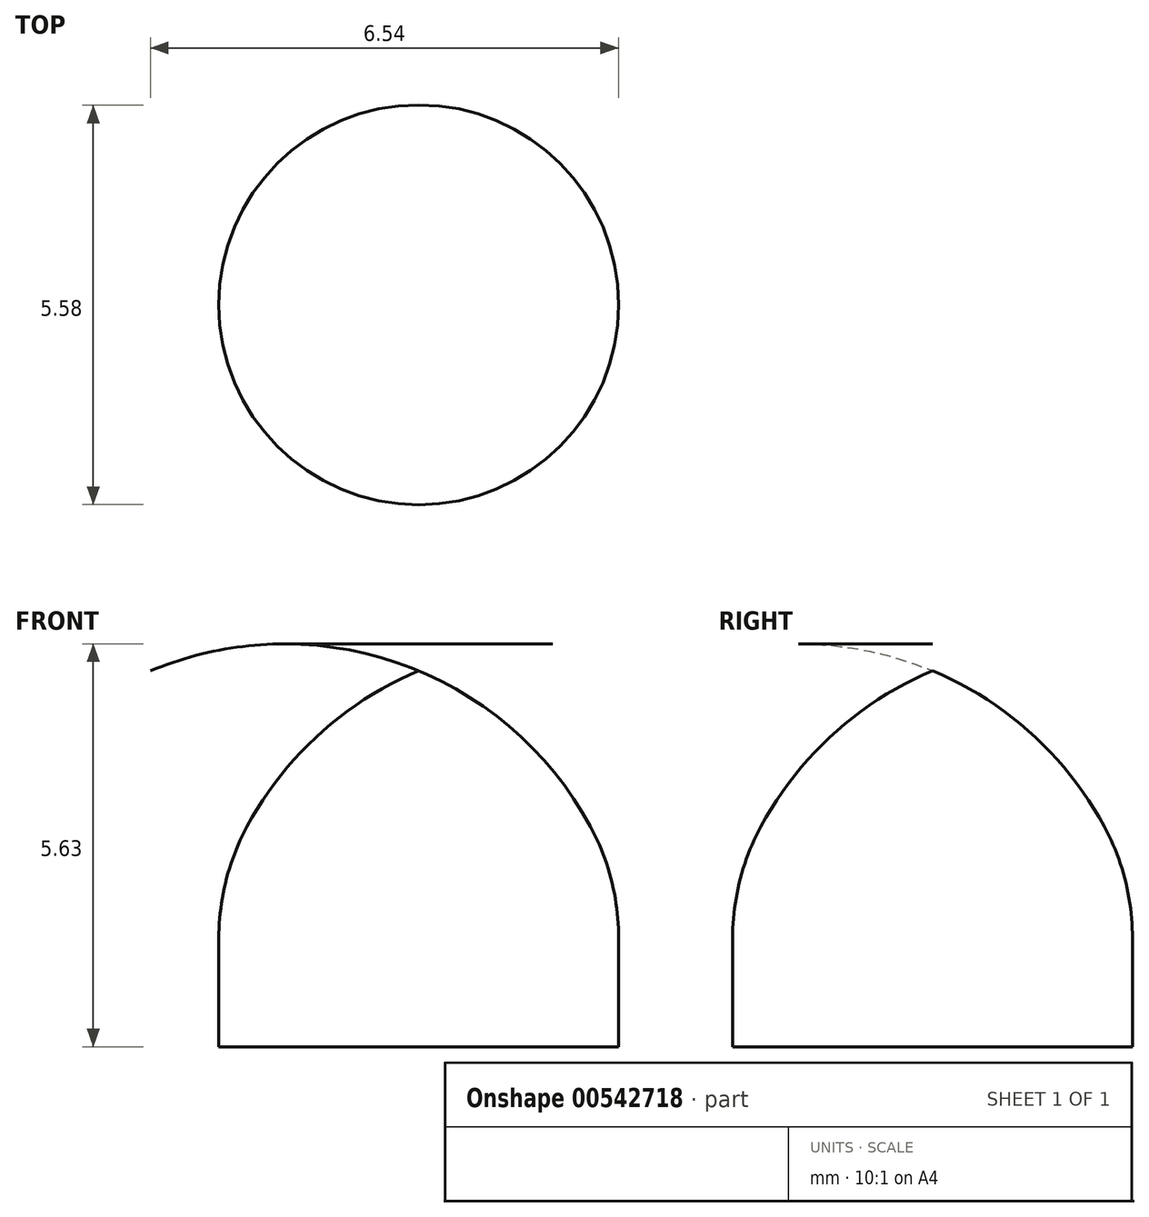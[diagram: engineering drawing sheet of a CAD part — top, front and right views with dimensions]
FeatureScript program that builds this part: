
annotation { "Feature Type Name" : "Feature", "Feature Type Description" : "" }
export const myFeature = defineFeature(function(context is Context, id is Id, definition is map)
    precondition{}
    {
        {
            var Q0;
            Q0=qCreatedBy(makeId("Front.planeOp"),FACE);
            var sketch = newSketch(context, id + "F0", { "sketchPlane" : qUnion([Q0])});
            skLineSegment(sketch, "E0", {"start": v(0, 0) * mm, "end": v(0, 5.25) * mm});
            skLineSegment(sketch, "E1", {"start": v(0, 0) * mm, "end": v(-2.8, 0) * mm});
            skLineSegment(sketch, "E2", {"start": v(-2.8, 0) * mm, "end": v(-2.8, 2.1) * mm});
            skArc(sketch, "E3", {"start": v(0, 5.25) * mm, "mid": v(-1.76, 4) * mm, "end": v(-2.8, 2.1) * mm});
            skSolve(sketch);
        }
        {
            var Q0;
            Q0 = qSketchRegion(id + "F0", true);
            var Q1;
            Q1=sQuery(id+"F0.wireOp",EDGE,"E0");
            revolve(context, id + "F1", {"entities" : qUnion([Q0]), "axis" : qUnion([Q1]), "revolveType" : RevolveType.FULL});
        }
        {
            var Q0;
            Q0=makeQuery(id+"F1.opRevolve","SWEPT_EDGE",EDGE,{"disambiguationData":[OSD([sQuery(id+"F0.wireOp",EDGE,"E2"),sQuery(id+"F0.wireOp",EDGE,"E3")])]});
            fillet(context, id + "F2", {"entities" : qUnion([Q0]), "radius" : 3.3 * mm, "tangentPropagation" : true, "allowEdgeOverflow" : false});
        }
    });
